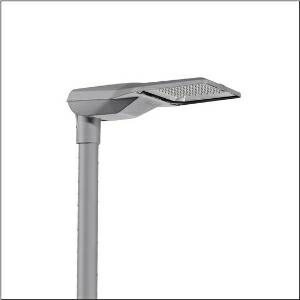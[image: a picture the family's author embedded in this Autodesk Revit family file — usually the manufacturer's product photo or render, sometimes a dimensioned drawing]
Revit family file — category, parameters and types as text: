
# Revit family: streetlight_sl_21_iq_midi___p0_8a_5xe3u31g08nb_121e
name_source: partatom
category: Lighting Fixtures
units: mm (PartAtom-declared; Revit-internal decimal feet)

## family parameters
Cut with Voids When Loaded = No
Host = Face
Light Source = No
Part Type = Normal
Room Calculation Point = No
Round Connector Dimension = Use Diameter
Shared = No

## types (1)
- --- (1 x LED, 23430 lm, 155.5 W, 3000K)
    Apparent Load = 155 VA
    CIE Flux Codes = 36 69 97 100 100
    Color Rendering = 70
    Color Temperature = 3000K
    Default Elevation = 1800 mm
    Description = Streetlight SL 21 iQ midi, mast luminaire, primary light control with lens, of PMMA, primary optical cover: cover, of toughened safety glass, transparent, light distribution: P0.8a, light emission: direct distribution, primary light characteristic: asymmetric, installation type: post-top, side-entry, LED, High Power LED, rated luminous flux: 23.430lm, luminous efficacy: 151lm/W, light colour: 730, colour temperature: 3000K, control gear: iQ Street-Remote, control: pre-setting: linear dimming characteristic, Street-Remote, Auto-Match, Temp-Guard, Lumen-Switch, Night-Set, Smart-Wire, Light-Fading, Desk-Remote (wireless, voltage-free reading and setting of iQ features in the workshop via application-optimized NFC function/RFID function), optimised constant luminous flux control (CLO 2.0), mains connection: 230..240V, AC, 50/60Hz, start of lifetime: 156W, end of service life: 162W, reduction: 69W, luminaire housing, of diecast aluminium, powder-coated, Siteco® metallic grey (DB 702S), corrosivity category C5 mid according to DIN EN ISO 12944, please order mast flange separately, inclination adjustable: 0°, 5°, 10°, 15°, sealing non-destructively replaceable, multi-level sealing system, length: 644mm, width: 335mm, height: 110mm, mast flange for spigot size: 42mm (side-entry): 5XC10008XM4, 60/48mm (side-entry/post-top): 5XC10108XM2, 76/60mm (side-entry/post-top): 5XC10108XM1, mounting height: 4..8m, protection rating (complete): IP66, insulation class (complete): insulation class II (safety insulation), certification: CE, ENEC, ENEC+, VDE, impact resistance: IK09, permissible operating ambient temperature for outdoor applications: -40..+50°C, standard-compliant lighting for roads and squares, packaging unit: 1 piece

Light Distribution: P0.8a
    Height = 111 mm
    Lamp = 1 x LED
    Lamp Light Flux = 23430 lm
    Lamp Power = 155.5 W
    Lamp count = 1
    Length = 644 mm
    Luminous efficacy = 151 lm/W
    Manufacturer = Siteco
    ModVariant = No
    Model = 5XE3U31G08NB
    Number of Poles = 1
    OnlyDefault = Yes
    Power Factor = 1
    Product Name = Streetlight SL 21 iQ midi | P0.8a
    Product group = mast luminaire | pylon top
    ProductGroupID = 6100
    Protection Class = Protection class II
    Protection Degree = IP 66
    RLX_Detail_Level = 1
    RLX_Emergency_Light_Flux = 0 lm
    RLX_Emergency_Type = 0
    RLX_Emergency_Type_DB = No
    RlxData = <blob elided: 90917 chars, md5=86300378>
    Socket = socket
    Standby Power = 0 W
    System Light Flux = 23431 lm
    System Power = 155 W
    Type Comments = factory setting: luminous flux: 100 % | dim-lin: 254 | 823 mA
    Type Image = l_1004298.jpg
    URL = http://relux.com
    VarID = @adj_068484
    Voltage = 0 V
    Weight = 0.00 kg
    Width = 336 mm

## geometry (parser evidence)
native form markers: Blend x4, Sweep x11
no freeform markers — native parametric forms only
